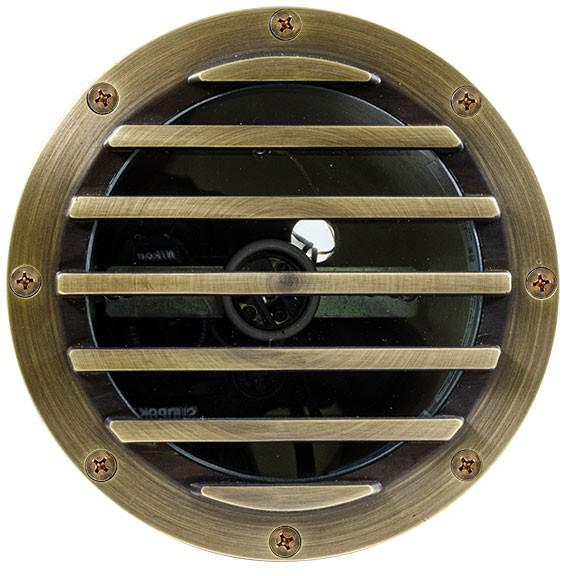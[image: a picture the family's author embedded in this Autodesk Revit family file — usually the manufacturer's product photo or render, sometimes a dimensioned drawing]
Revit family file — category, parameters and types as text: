
# Revit family: Alcon-9044-Revit-Family
name_source: partatom
category: Luminarias
units: mm (PartAtom-declared; Revit-internal decimal feet)

## family parameters
Anfitrión = Cara
Compartido = No
Corte con vacíos al cargar = No
Cota de conector redondo = Usar diámetro
Mantener orientación de anotación = No
Origen de luz = Sí
Punto de cálculo de habitación = No
Tipo de pieza = Normal

## types (1)
- Alcon-9044-Revit-Family
    Cambio de temperatura de color de luz atenuada = <Ninguno>
    Elevación por defecto = 4' - 0"
    Fabricante = Alcon Lighting
    Filtro de color = 16777215
    LENS GLASS = Glass
    Link to IES File = https://www.alconlighting.com
    Longitud de símbolo de origen de luz = 10' - 0"
    Modelo = Alcon Lighting 9044
    Product Data URL = https://www.alconlighting.com
    Product Page = https://www.alconlighting.com
    TOP FINISH = <Por categoría>
    URL = https://www.alconlighting.com
    Ángulo de campo de foco = 90.00°
    Ángulo de enfoque = 30.00°
    Ángulo de inclinación = 60.00°

## geometry (parser evidence)
native form markers: Sweep x3
no freeform markers — native parametric forms only
